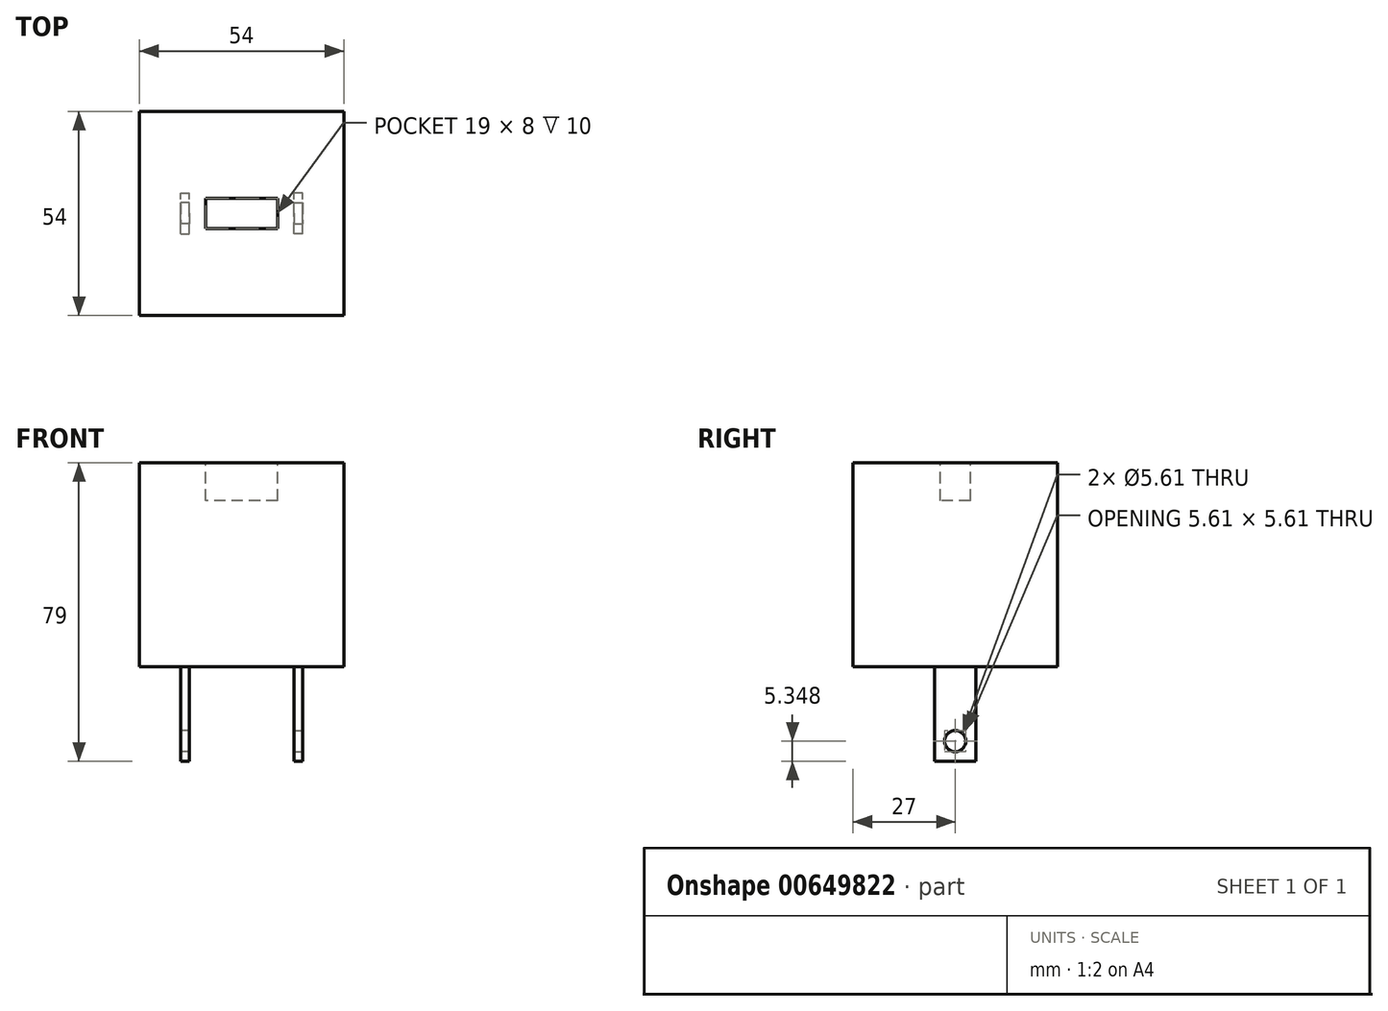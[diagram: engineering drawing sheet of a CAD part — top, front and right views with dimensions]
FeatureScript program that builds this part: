
annotation { "Feature Type Name" : "Feature", "Feature Type Description" : "" }
export const myFeature = defineFeature(function(context is Context, id is Id, definition is map)
    precondition{}
    {
        {
            var Q0;
            Q0=qCreatedBy(makeId("Top.planeOp"),FACE);
            var sketch = newSketch(context, id + "F0", { "sketchPlane" : qUnion([Q0])});
            skLineSegment(sketch, "E0.bottom", {"start": v(27, 27) * mm, "end": v(-27, 27) * mm});
            skLineSegment(sketch, "E0.top", {"start": v(27, -27) * mm, "end": v(-27, -27) * mm});
            skLineSegment(sketch, "E0.left", {"start": v(27, 27) * mm, "end": v(27, -27) * mm});
            skLineSegment(sketch, "E0.right", {"start": v(-27, 27) * mm, "end": v(-27, -27) * mm});
            skPoint(sketch, "E0.middle", {"position": v(0, 0) * mm});
            skSolve(sketch);
        }
        {
            var Q0;
            Q0=makeQuery(id+"F0.imprint","IMPRINT",FACE,{"disambiguationData":[TD([[makeQuery(id+"F0.imprint","IMPRINT",EDGE,{"derivedFrom":sQuery(id+"F0.wireOp",EDGE,"E0.bottom")}),1.0]])]});
            extrude(context, id + "F1", {"entities" : qUnion([Q0]), "depth" : 54 * mm, "offsetDistance" : 25 * mm});
        }
        {
            var Q0;
            Q0=makeQuery(id+"F1.opExtrude","CAP_FACE",FACE,{"disambiguationData":[OSD([sQuery(id+"F0.wireOp",EDGE,"E0.bottom"),sQuery(id+"F0.wireOp",EDGE,"E0.top"),sQuery(id+"F0.wireOp",EDGE,"E0.left"),sQuery(id+"F0.wireOp",EDGE,"E0.right")])],"isStart":false});
            var sketch = newSketch(context, id + "F2", { "sketchPlane" : qUnion([Q0])});
            skLineSegment(sketch, "E1.bottom", {"start": v(9.5, 4) * mm, "end": v(-9.5, 4) * mm});
            skLineSegment(sketch, "E1.top", {"start": v(9.5, -4) * mm, "end": v(-9.5, -4) * mm});
            skLineSegment(sketch, "E1.left", {"start": v(9.5, 4) * mm, "end": v(9.5, -4) * mm});
            skLineSegment(sketch, "E1.right", {"start": v(-9.5, 4) * mm, "end": v(-9.5, -4) * mm});
            skPoint(sketch, "E1.middle", {"position": v(0, 0) * mm});
            skSolve(sketch);
        }
        {
            var Q0;
            Q0=makeQuery(id+"F2.imprint","IMPRINT",FACE,{"disambiguationData":[TD([[makeQuery(id+"F2.imprint","IMPRINT",EDGE,{"derivedFrom":sQuery(id+"F2.wireOp",EDGE,"E1.bottom")}),1.0]])]});
            extrude(context, id + "F3", {"entities" : qUnion([Q0]), "operationType" : NewBodyOperationType.REMOVE, "oppositeDirection" : true, "depth" : 10 * mm, "offsetDistance" : 25 * mm});
        }
        {
            var Q0;
            Q0=makeQuery(id+"F1.opExtrude","CAP_FACE",FACE,{"disambiguationData":[OSD([sQuery(id+"F0.wireOp",EDGE,"E0.bottom"),sQuery(id+"F0.wireOp",EDGE,"E0.top"),sQuery(id+"F0.wireOp",EDGE,"E0.left"),sQuery(id+"F0.wireOp",EDGE,"E0.right")])],"isStart":true});
            var sketch = newSketch(context, id + "F4", { "sketchPlane" : qUnion([Q0])});
            skLineSegment(sketch, "E2.bottom", {"start": v(-16.13, 5.42) * mm, "end": v(-13.88, 5.42) * mm});
            skLineSegment(sketch, "E2.top", {"start": v(-16.13, -5.42) * mm, "end": v(-13.88, -5.42) * mm});
            skLineSegment(sketch, "E2.left", {"start": v(-16.13, 5.42) * mm, "end": v(-16.13, -5.42) * mm});
            skLineSegment(sketch, "E2.right", {"start": v(-13.88, 5.42) * mm, "end": v(-13.88, -5.42) * mm});
            skPoint(sketch, "E2.middle", {"position": v(-15, 0) * mm});
            skSolve(sketch);
        }
        {
            var Q0;
            Q0=makeQuery(id+"F4.imprint","IMPRINT",FACE,{"disambiguationData":[TD([[makeQuery(id+"F4.imprint","IMPRINT",EDGE,{"derivedFrom":sQuery(id+"F4.wireOp",EDGE,"E2.bottom")}),-1.0]])]});
            extrude(context, id + "F5", {"entities" : qUnion([Q0]), "operationType" : NewBodyOperationType.ADD, "depth" : 25 * mm, "offsetDistance" : 25 * mm});
        }
        {
            var Q0;
            Q0=makeQuery(id+"F5.opExtrude","SWEPT_FACE",FACE,{"disambiguationData":[OSD([sQuery(id+"F4.wireOp",EDGE,"E2.left")])]});
            var sketch = newSketch(context, id + "F6", { "sketchPlane" : qUnion([Q0])});
            skCircle(sketch, "E3", {"center": v(0, -19.65) * mm, "radius": 2.8 * mm});
            skPoint(sketch, "E3.centerSnap0", {"position": v(0, -25) * mm});
            skSolve(sketch);
        }
        {
            var Q0;
            Q0=makeQuery(id+"F6.imprint","IMPRINT",FACE,{"disambiguationData":[TD([[makeQuery(id+"F6.imprint","IMPRINT",EDGE,{"derivedFrom":sQuery(id+"F6.wireOp",EDGE,"E3")}),1.0]])]});
            extrude(context, id + "F7", {"entities" : qUnion([Q0]), "operationType" : NewBodyOperationType.REMOVE, "oppositeDirection" : true, "depth" : 3 * mm, "offsetDistance" : 25 * mm});
        }
        {
            var Q0;
            Q0=makeQuery(id+"F1.opExtrude","SWEPT_BODY",BODY,{"disambiguationData":[OSD([sQuery(id+"F0.wireOp",EDGE,"E0.bottom"),sQuery(id+"F0.wireOp",EDGE,"E0.top"),sQuery(id+"F0.wireOp",EDGE,"E0.left"),sQuery(id+"F0.wireOp",EDGE,"E0.right")])]});
            var Q1;
            Q1=qCreatedBy(makeId("Right.planeOp"),FACE);
            mirror(context, id + "F8", {"operationType" : NewBodyOperationType.ADD, "entities" : qUnion([Q0]), "mirrorPlane" : qUnion([Q1])});
        }
    });
